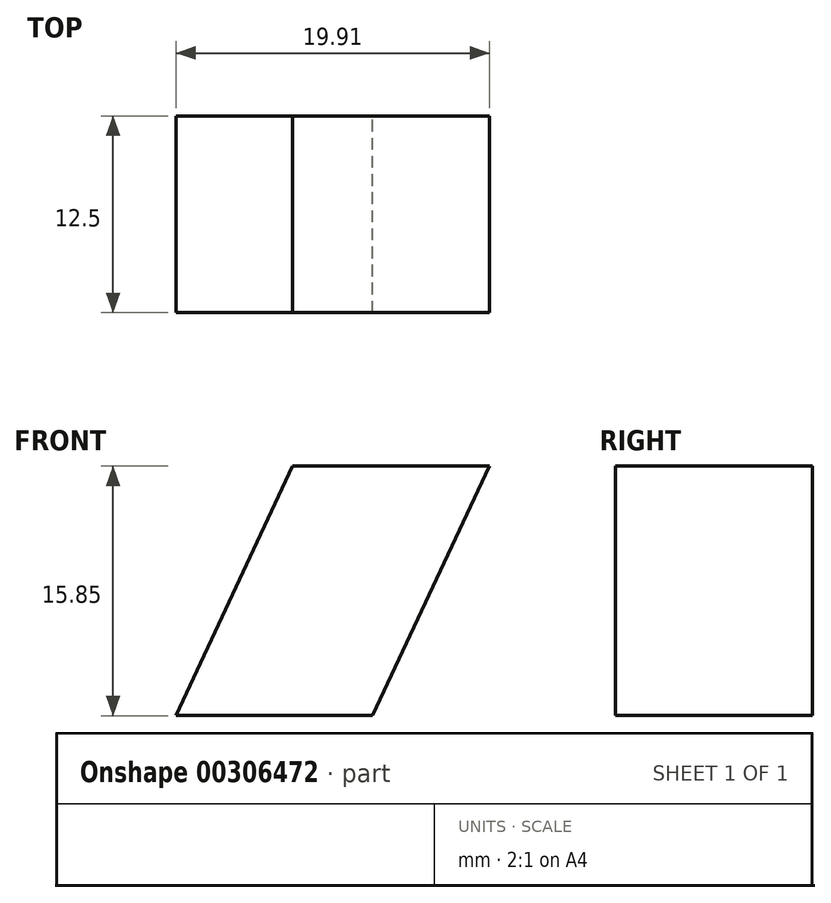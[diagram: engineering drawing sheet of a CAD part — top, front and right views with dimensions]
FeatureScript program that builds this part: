
annotation { "Feature Type Name" : "Feature", "Feature Type Description" : "" }
export const myFeature = defineFeature(function(context is Context, id is Id, definition is map)
    precondition{}
    {
        {
            var Q0;
            Q0=qCreatedBy(makeId("Front.planeOp"),FACE);
            var sketch = newSketch(context, id + "F0", { "sketchPlane" : qUnion([Q0])});
            skLineSegment(sketch, "E0", {"start": v(-37.3, -38.06) * mm, "end": v(-22.48, -6.35) * mm});
            skLineSegment(sketch, "E1", {"start": v(-22.48, -6.35) * mm, "end": v(2.52, -6.35) * mm});
            skLineSegment(sketch, "E2", {"start": v(-37.3, -38.06) * mm, "end": v(-12.3, -38.06) * mm});
            skLineSegment(sketch, "E3", {"start": v(-12.3, -38.06) * mm, "end": v(2.52, -6.35) * mm});
            skSolve(sketch);
        }
        {
            var Q0;
            Q0=makeQuery(id+"F0.imprint","IMPRINT",FACE,{"disambiguationData":[TD([[makeQuery(id+"F0.imprint","IMPRINT",EDGE,{"derivedFrom":sQuery(id+"F0.wireOp",EDGE,"E0")}),-1.0]])]});
            extrude(context, id + "F1", {"entities" : qUnion([Q0]), "depth" : 25 * mm});
        }
        {
            var Q0;
            Q0=makeQuery(id+"F1.opExtrude","SWEPT_BODY",BODY,{"disambiguationData":[OSD([sQuery(id+"F0.wireOp",EDGE,"E0"),sQuery(id+"F0.wireOp",EDGE,"E1"),sQuery(id+"F0.wireOp",EDGE,"E2"),sQuery(id+"F0.wireOp",EDGE,"E3")])]});
            var Q1;
            Q1=qCreatedBy(makeId("Origin.pointOp"),VERTEX);
            transform(context, id + "F2", {"entities" : qUnion([Q0]), "transformType" : TransformType.SCALE_UNIFORMLY, "scale" : 0.5, "scalePoint" : qUnion([Q1]), "makeCopy" : false});
        }
    });
